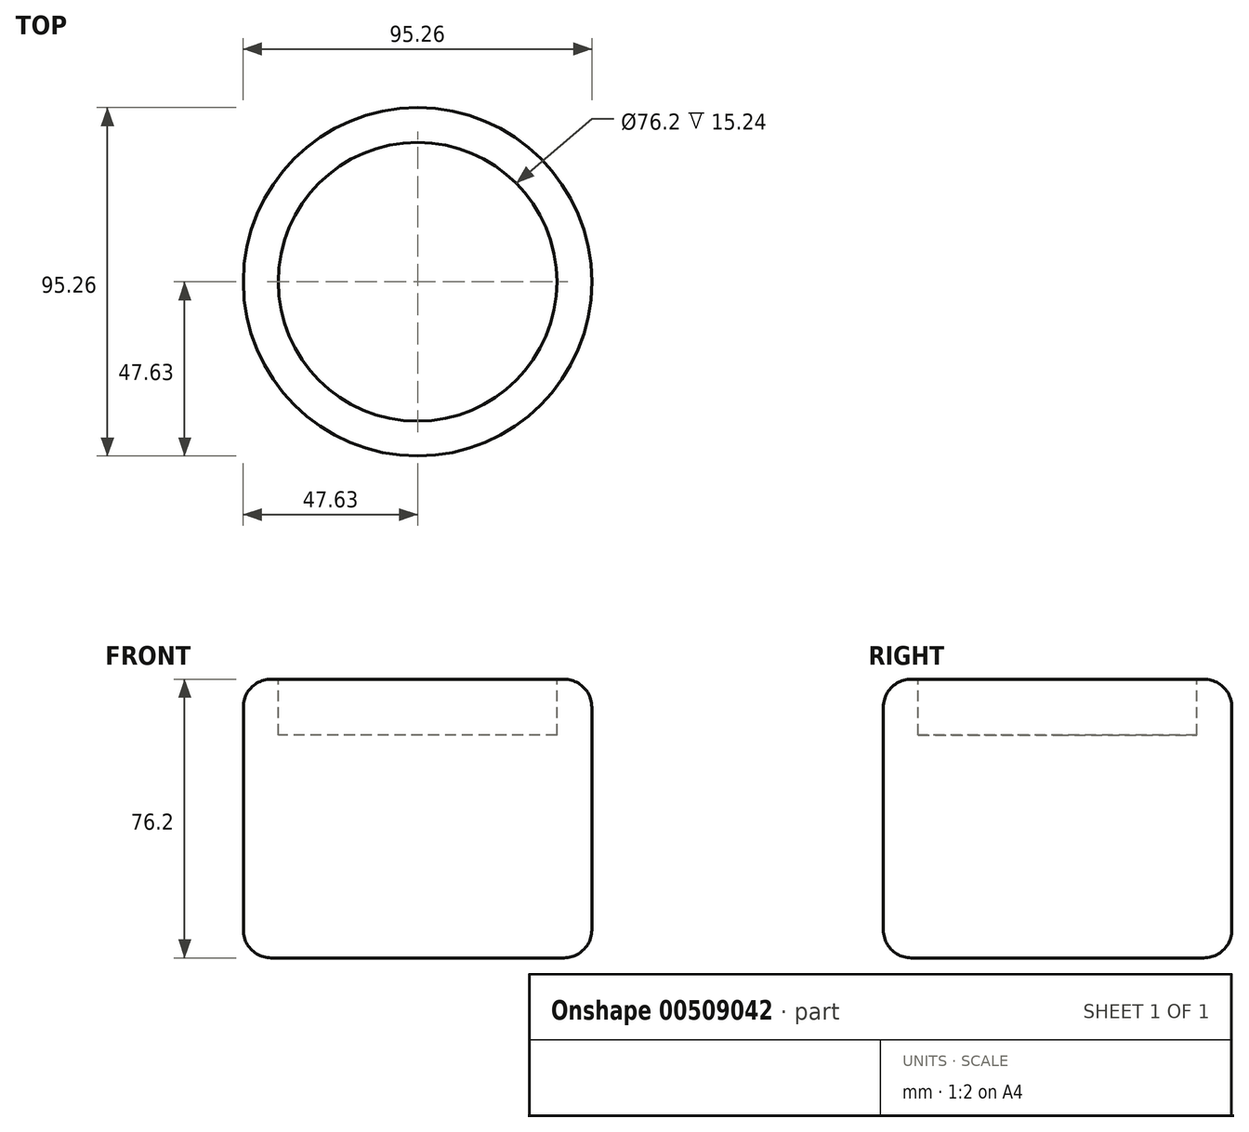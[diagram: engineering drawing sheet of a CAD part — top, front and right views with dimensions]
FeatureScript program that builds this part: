
annotation { "Feature Type Name" : "Feature", "Feature Type Description" : "" }
export const myFeature = defineFeature(function(context is Context, id is Id, definition is map)
    precondition{}
    {
        {
            var Q0;
            Q0=qCreatedBy(makeId("Top.planeOp"),FACE);
            var sketch = newSketch(context, id + "F0", { "sketchPlane" : qUnion([Q0])});
            skCircle(sketch, "E0", {"center": v(0, 0) * mm, "radius": 53.82 * mm});
            skCircle(sketch, "E1", {"center": v(0, 0) * mm, "radius": 47.63 * mm});
            skSolve(sketch);
        }
        {
            var Q0;
            Q0=makeQuery(id+"F0.imprint","IMPRINT",FACE,{"disambiguationData":[TD([[makeQuery(id+"F0.imprint","IMPRINT",EDGE,{"derivedFrom":sQuery(id+"F0.wireOp",EDGE,"E1")}),1.0]])]});
            extrude(context, id + "F1", {"entities" : qUnion([Q0]), "depth" : 76.2 * mm});
        }
        {
            var Q0;
            Q0=makeQuery(id+"F1.opExtrude","CAP_FACE",FACE,{"disambiguationData":[OSD([sQuery(id+"F0.wireOp",EDGE,"E1")])],"isStart":false});
            var sketch = newSketch(context, id + "F2", { "sketchPlane" : qUnion([Q0])});
            skSolve(sketch);
        }
        {
            var Q0;
            Q0=makeQuery(id+"F2.imprint","IMPRINT",FACE,{"disambiguationData":[TD([[makeQuery(id+"F2.imprint","IMPRINT",EDGE,{"derivedFrom":makeQuery(id+"F1.opExtrude","CAP_EDGE",EDGE,{"disambiguationData":[OSD([sQuery(id+"F0.wireOp",EDGE,"E1")])],"isStart":false})}),1.0]])]});
            var sketch = newSketch(context, id + "F3", { "sketchPlane" : qUnion([Q0])});
            skCircle(sketch, "E2", {"center": v(0, 0) * mm, "radius": 19.57 * mm});
            skSolve(sketch);
        }
        {
            var Q0;
            Q0=sQuery(id+"F3.wireOp",VERTEX,"E2.center");
            var Q1;
            Q1=makeQuery(id+"F1.opExtrude","SWEPT_BODY",BODY,{"disambiguationData":[OSD([sQuery(id+"F0.wireOp",EDGE,"E1")])]});
            hole(context, id + "F4", {"style" : HoleStyle.SIMPLE, "endStyle" : HoleEndStyle.THROUGH, "holeDiameter" : 76.2 * mm, "isTappedThrough" : true, "tappedDepth" : 12.7 * mm, "tapClearance" : 3, "locations" : qUnion([Q0]), "scope" : qUnion([Q1])});
        }
        {
            var Q0;
            Q0=makeQuery(id+"F1.opExtrude","CAP_EDGE",EDGE,{"disambiguationData":[OSD([sQuery(id+"F0.wireOp",EDGE,"E1")])],"isStart":false});
            fillet(context, id + "F5", {"entities" : qUnion([Q0]), "radius" : 7.62 * mm, "tangentPropagation" : true, "allowEdgeOverflow" : false});
        }
        {
            var Q0;
            Q0=makeQuery(id+"F1.opExtrude","CAP_EDGE",EDGE,{"disambiguationData":[OSD([sQuery(id+"F0.wireOp",EDGE,"E1")])],"isStart":true});
            fillet(context, id + "F6", {"entities" : qUnion([Q0]), "radius" : 7.62 * mm, "tangentPropagation" : true, "allowEdgeOverflow" : false});
        }
        {
            var Q0;
            Q0=qCreatedBy(makeId("Top.planeOp"),FACE);
            var sketch = newSketch(context, id + "F7", { "sketchPlane" : qUnion([Q0])});
            skCircle(sketch, "E3", {"center": v(0, 0) * mm, "radius": 38.1 * mm});
            skSolve(sketch);
        }
        {
            var Q0;
            Q0 = qSketchRegion(id + "F7", true);
            extrude(context, id + "F8", {"entities" : qUnion([Q0]), "operationType" : NewBodyOperationType.ADD, "depth" : 60.96 * mm});
        }
    });
